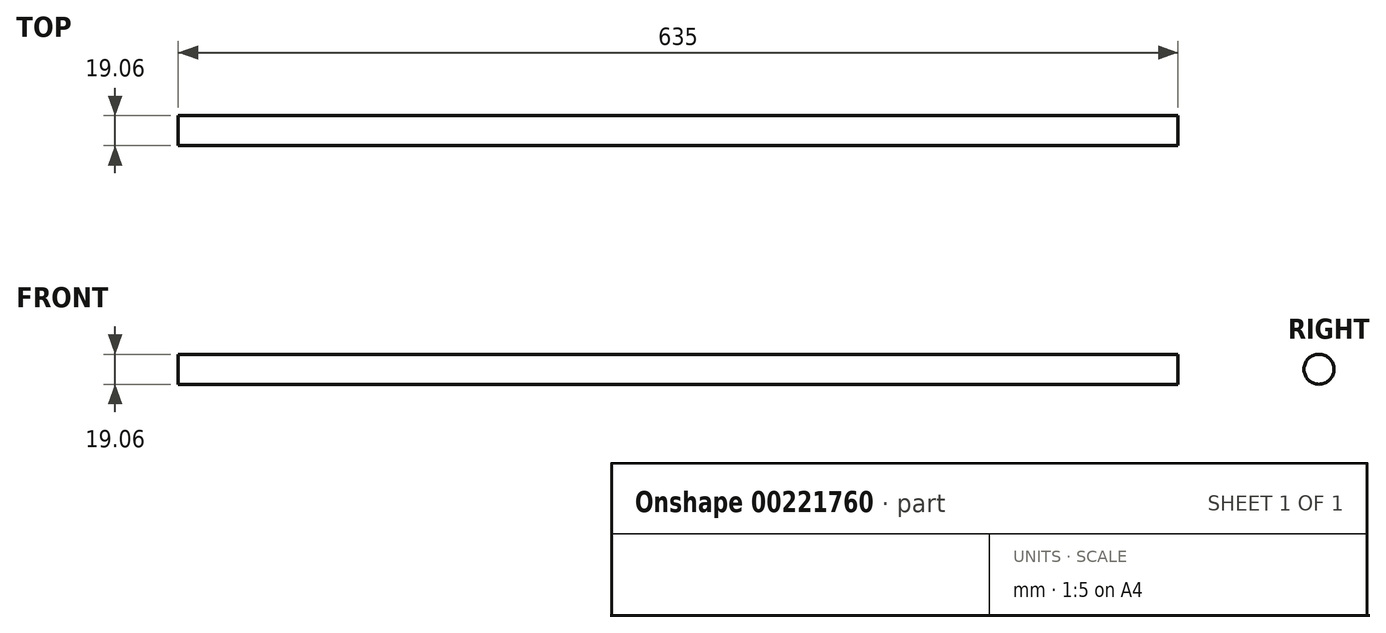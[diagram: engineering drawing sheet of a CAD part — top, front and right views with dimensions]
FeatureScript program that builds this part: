
annotation { "Feature Type Name" : "Feature", "Feature Type Description" : "" }
export const myFeature = defineFeature(function(context is Context, id is Id, definition is map)
    precondition{}
    {
        {
            var Q0;
            Q0=qCreatedBy(makeId("Right.planeOp"),FACE);
            var sketch = newSketch(context, id + "F0", { "sketchPlane" : qUnion([Q0])});
            skCircle(sketch, "E0", {"center": v(0, 0) * mm, "radius": 9.53 * mm});
            skSolve(sketch);
        }
        {
            var Q0;
            Q0 = qSketchRegion(id + "F0", true);
            extrude(context, id + "F1", {"entities" : qUnion([Q0]), "depth" : 635 * mm});
        }
    });
